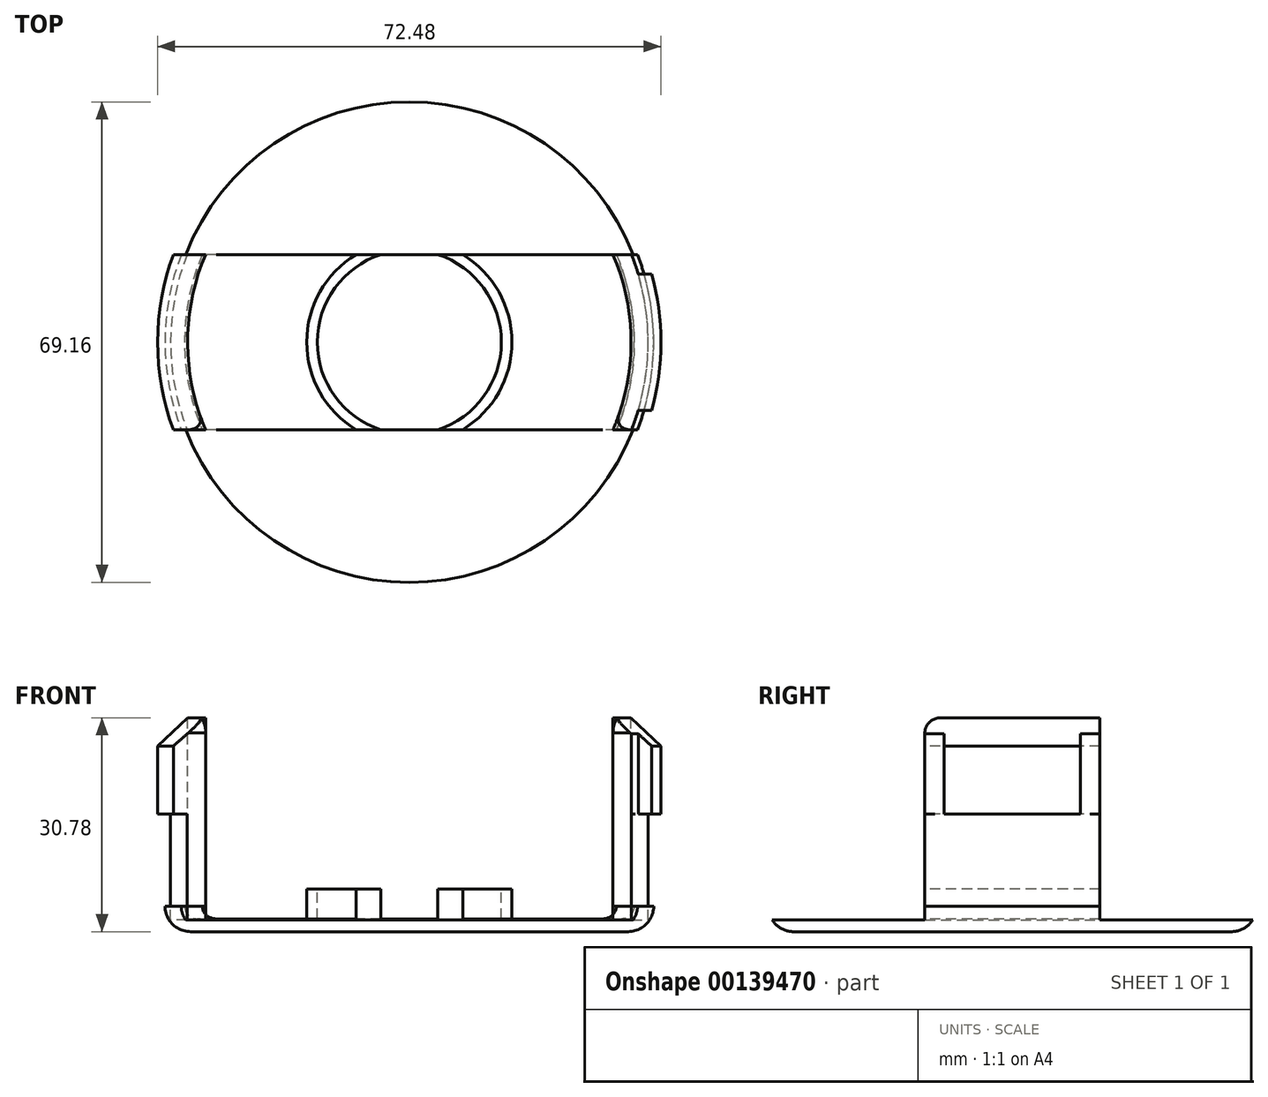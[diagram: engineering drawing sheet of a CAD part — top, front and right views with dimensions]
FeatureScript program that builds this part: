
annotation { "Feature Type Name" : "Feature", "Feature Type Description" : "" }
export const myFeature = defineFeature(function(context is Context, id is Id, definition is map)
    precondition{}
    {
        {
            var Q0;
            Q0=qCreatedBy(makeId("Front.planeOp"),FACE);
            var sketch = newSketch(context, id + "F0", { "sketchPlane" : qUnion([Q0])});
            skLineSegment(sketch, "E0.top", {"start": v(34, 4.4) * mm, "end": v(32.36, 4.4) * mm});
            skLineSegment(sketch, "E0.right", {"start": v(32.36, 0) * mm, "end": v(32.36, 4.4) * mm});
            skPoint(sketch, "E1", {"position": v(0, -3.68) * mm});
            skLineSegment(sketch, "E2", {"start": v(0, -3.68) * mm, "end": v(31.5, -3.68) * mm});
            skLineSegment(sketch, "E3", {"start": v(35.18, 0) * mm, "end": v(35.18, 0) * mm});
            skLineSegment(sketch, "E4", {"start": v(0, -3.68) * mm, "end": v(0, -1.84) * mm});
            skLineSegment(sketch, "E5", {"start": v(0, -1.84) * mm, "end": v(13.25, -1.84) * mm});
            skPoint(sketch, "E5.endSnap0", {"position": v(35.18, -1.84) * mm});
            skLineSegment(sketch, "E6.trimOffspring", {"start": v(14.77, -1.84) * mm, "end": v(30.53, -1.84) * mm});
            skPoint(sketch, "E7.visualSharp", {"position": v(35.18, -3.68) * mm});
            skArc(sketch, "E7.filletArc", {"start": v(31.5, -3.68) * mm, "mid": v(34.1, -2.6) * mm, "end": v(35.18, 0) * mm});
            skPoint(sketch, "E8.visualSharp", {"position": v(32.36, -1.84) * mm});
            skLineSegment(sketch, "E9", {"start": v(35.18, 0) * mm, "end": v(34, 0) * mm});
            skLineSegment(sketch, "E10", {"start": v(34, 0) * mm, "end": v(34, 4.4) * mm});
            skLineSegment(sketch, "E11", {"start": v(0, 4.4) * mm, "end": v(0, -3.68) * mm, "construction": true});
            skLineSegment(sketch, "E12", {"start": v(34, 3.6) * mm, "end": v(0, 3.6) * mm, "construction": true});
            skArc(sketch, "E13", {"start": v(30.53, -1.84) * mm, "mid": v(31.83, -1.3) * mm, "end": v(32.36, 0) * mm});
            skLineSegment(sketch, "E14", {"start": v(13.25, 2.46) * mm, "end": v(14.77, 2.46) * mm});
            skLineSegment(sketch, "E15", {"start": v(13.25, 2.46) * mm, "end": v(13.25, -1.84) * mm});
            skLineSegment(sketch, "E16", {"start": v(14.77, 2.46) * mm, "end": v(14.77, -1.84) * mm});
            skSolve(sketch);
        }
        {
            var Q0;
            Q0=makeQuery(id+"F0.imprint","IMPRINT",FACE,{"disambiguationData":[TD([[makeQuery(id+"F0.imprint","IMPRINT",EDGE,{"derivedFrom":sQuery(id+"F0.wireOp",EDGE,"E0.top")}),1.0]])]});
            var Q1;
            Q1=sQuery(id+"F0.wireOp",EDGE,"E11");
            revolve(context, id + "F1", {"entities" : qUnion([Q0]), "axis" : qUnion([Q1]), "revolveType" : RevolveType.FULL});
        }
        {
            var Q0;
            Q0=qCreatedBy(makeId("Top.planeOp"),FACE);
            var sketch = newSketch(context, id + "F2", { "sketchPlane" : qUnion([Q0])});
            skLineSegment(sketch, "E17", {"start": v(-42.99, 0) * mm, "end": v(-42.99, 15.25) * mm});
            skLineSegment(sketch, "E18", {"start": v(-19.65, 0) * mm, "end": v(-19.65, -15.25) * mm});
            skLineSegment(sketch, "E19", {"start": v(-19.65, -15.25) * mm, "end": v(-42.99, -15.25) * mm});
            skLineSegment(sketch, "E20", {"start": v(-42.99, -15.25) * mm, "end": v(-42.99, 0) * mm});
            skLineSegment(sketch, "E21", {"start": v(-42.99, 15.25) * mm, "end": v(-19.65, 15.25) * mm});
            skLineSegment(sketch, "E22", {"start": v(-19.65, 15.25) * mm, "end": v(-19.65, 0) * mm});
            skLineSegment(sketch, "E23.MirrorCS", {"start": v(42.99, 15.25) * mm, "end": v(19.65, 15.25) * mm});
            skLineSegment(sketch, "E24.MirrorCS", {"start": v(19.65, 15.25) * mm, "end": v(19.65, 0) * mm});
            skLineSegment(sketch, "E25.MirrorCS", {"start": v(42.99, 0) * mm, "end": v(42.99, 15.25) * mm});
            skLineSegment(sketch, "E26.MirrorCS", {"start": v(42.99, -15.25) * mm, "end": v(42.99, 0) * mm});
            skLineSegment(sketch, "E27.MirrorCS", {"start": v(19.65, -15.25) * mm, "end": v(42.99, -15.25) * mm});
            skLineSegment(sketch, "E28.MirrorCS", {"start": v(19.65, 0) * mm, "end": v(19.65, -15.25) * mm});
            skSolve(sketch);
        }
        {
            var Q0;
            Q0=makeQuery(id+"F2.imprint","IMPRINT",FACE,{"disambiguationData":[TD([[makeQuery(id+"F2.imprint","IMPRINT",EDGE,{"derivedFrom":sQuery(id+"F2.wireOp",EDGE,"E17")}),-1.0]])]});
            var Q1;
            Q1=makeQuery(id+"F2.imprint","IMPRINT",FACE,{"disambiguationData":[TD([[makeQuery(id+"F2.imprint","IMPRINT",EDGE,{"derivedFrom":sQuery(id+"F2.wireOp",EDGE,"E23.MirrorCS")}),1.0]])]});
            extrude(context, id + "F3", {"entities" : qUnion([Q0, Q1]), "operationType" : NewBodyOperationType.REMOVE, "endBound" : BoundingType.THROUGH_ALL, "depth" : 25 * mm});
        }
        {
            var Q0;
            Q0=qCreatedBy(makeId("Front.planeOp"),FACE);
            var sketch = newSketch(context, id + "F4", { "sketchPlane" : qUnion([Q0])});
            skLineSegment(sketch, "E29.left", {"start": v(34.38, 0) * mm, "end": v(34.38, 13.22) * mm});
            skLineSegment(sketch, "E29.right", {"start": v(31.92, -1.9) * mm, "end": v(31.92, 27.1) * mm});
            skLineSegment(sketch, "E30.bottom", {"start": v(34.38, 13.22) * mm, "end": v(36.24, 13.22) * mm});
            skLineSegment(sketch, "E30.right", {"start": v(36.24, 13.22) * mm, "end": v(36.24, 23.05) * mm});
            skLineSegment(sketch, "E31", {"start": v(31.92, 27.1) * mm, "end": v(36.24, 23.05) * mm});
            skLineSegment(sketch, "E32", {"start": v(0, 35.2) * mm, "end": v(0, 1.71) * mm, "construction": true});
            skLineSegment(sketch, "E33", {"start": v(34.38, 8.25) * mm, "end": v(0, 8.25) * mm, "construction": true});
            skLineSegment(sketch, "E34", {"start": v(36.24, 18.13) * mm, "end": v(31.92, 18.13) * mm, "construction": true});
            skLineSegment(sketch, "E35", {"start": v(34.38, 0) * mm, "end": v(34.38, -2) * mm});
            skLineSegment(sketch, "E36", {"start": v(34.38, -2) * mm, "end": v(31.92, -2) * mm});
            skLineSegment(sketch, "E37", {"start": v(31.92, -2) * mm, "end": v(31.92, -1.9) * mm});
            skSolve(sketch);
        }
        {
            var Q0;
            Q0=makeQuery(id+"F4.imprint","IMPRINT",FACE,{"disambiguationData":[TD([[makeQuery(id+"F4.imprint","IMPRINT",EDGE,{"derivedFrom":sQuery(id+"F4.wireOp",EDGE,"E29.left")}),1.0]])]});
            var Q1;
            Q1=sQuery(id+"F4.wireOp",EDGE,"E32");
            revolve(context, id + "F5", {"entities" : qUnion([Q0]), "axis" : qUnion([Q1]), "revolveType" : RevolveType.FULL});
        }
        {
            var Q0;
            Q0=makeQuery(id+"F5.opRevolve","SWEPT_FACE",FACE,{"disambiguationData":[OSD([sQuery(id+"F4.wireOp",EDGE,"E36")])]});
            var sketch = newSketch(context, id + "F6", { "sketchPlane" : qUnion([Q0])});
            skLineSegment(sketch, "E38.bottom", {"start": v(-47.17, -12.61) * mm, "end": v(51.45, -12.61) * mm});
            skLineSegment(sketch, "E38.top", {"start": v(-47.17, -53.6) * mm, "end": v(51.45, -53.6) * mm});
            skLineSegment(sketch, "E38.left", {"start": v(-47.17, -12.61) * mm, "end": v(-47.17, -53.6) * mm});
            skLineSegment(sketch, "E38.right", {"start": v(51.45, -12.6) * mm, "end": v(51.45, -53.6) * mm});
            skLineSegment(sketch, "E39", {"start": v(51.45, 0) * mm, "end": v(51.45, 0) * mm});
            skLineSegment(sketch, "E40.MirrorCS", {"start": v(-47.17, 12.6) * mm, "end": v(51.45, 12.61) * mm});
            skLineSegment(sketch, "E41.MirrorCS", {"start": v(-47.17, 53.6) * mm, "end": v(51.45, 53.6) * mm});
            skLineSegment(sketch, "E42.MirrorCS", {"start": v(51.45, 12.61) * mm, "end": v(51.45, 53.6) * mm});
            skLineSegment(sketch, "E43.MirrorCS", {"start": v(-47.17, 12.6) * mm, "end": v(-47.17, 53.6) * mm});
            skLineSegment(sketch, "E44", {"start": v(51.45, -12.61) * mm, "end": v(51.45, 0) * mm});
            skLineSegment(sketch, "E45", {"start": v(51.45, 12.61) * mm, "end": v(51.45, 0) * mm});
            skSolve(sketch);
        }
        {
            var Q0;
            {var subQ0=sQuery(id+"F6.wireOp",EDGE,"E40.MirrorCS");var subQ1=sQuery(id+"F4.wireOp",EDGE,"E36");var subQ2=makeQuery(id+"F5.opRevolve","SWEPT_EDGE",EDGE,{"disambiguationData":[OSD([sQuery(id+"F4.wireOp",EDGE,"E35"),subQ1])]});var subQ3=makeQuery(id+"F6.imprint","INTERSECT",VERTEX,{"disambiguationData":[OD(0.0)],"derivedFrom":[subQ2,subQ0]});Q0=makeQuery(id+"F6.imprint","IMPRINT",FACE,{"disambiguationData":[TD([[makeQuery(id+"F6.imprint","IMPRINT",EDGE,{"disambiguationData":[TD([[subQ3,-1.0]])],"derivedFrom":subQ0}),1.0]])]});}
            var Q1;
            {var subQ0=sQuery(id+"F6.wireOp",EDGE,"E40.MirrorCS");var subQ1=makeQuery(id+"F5.opRevolve","SWEPT_EDGE",EDGE,{"disambiguationData":[OSD([sQuery(id+"F4.wireOp",EDGE,"E36"),sQuery(id+"F4.wireOp",EDGE,"E37")])]});var subQ2=makeQuery(id+"F6.imprint","INTERSECT",VERTEX,{"disambiguationData":[OD(0.0)],"derivedFrom":[subQ1,subQ0]});Q1=makeQuery(id+"F6.imprint","IMPRINT",FACE,{"disambiguationData":[TD([[makeQuery(id+"F6.imprint","IMPRINT",EDGE,{"disambiguationData":[TD([[subQ2,-1.0]])],"derivedFrom":subQ0}),1.0]])]});}
            var Q2;
            Q2=makeQuery(id+"F6.imprint","IMPRINT",FACE,{"disambiguationData":[TD([[makeQuery(id+"F6.imprint","IMPRINT",EDGE,{"derivedFrom":sQuery(id+"F6.wireOp",EDGE,"E41.MirrorCS")}),-1.0]])]});
            var Q3;
            Q3=makeQuery(id+"F6.imprint","IMPRINT",FACE,{"disambiguationData":[TD([[makeQuery(id+"F6.imprint","IMPRINT",EDGE,{"derivedFrom":sQuery(id+"F6.wireOp",EDGE,"E38.top")}),1.0]])]});
            var Q4;
            {var subQ0=sQuery(id+"F6.wireOp",EDGE,"E38.bottom");var subQ1=sQuery(id+"F4.wireOp",EDGE,"E36");var subQ2=makeQuery(id+"F5.opRevolve","SWEPT_EDGE",EDGE,{"disambiguationData":[OSD([sQuery(id+"F4.wireOp",EDGE,"E35"),subQ1])]});var subQ3=makeQuery(id+"F6.imprint","INTERSECT",VERTEX,{"disambiguationData":[OD(0.0)],"derivedFrom":[subQ2,subQ0]});Q4=makeQuery(id+"F6.imprint","IMPRINT",FACE,{"disambiguationData":[TD([[makeQuery(id+"F6.imprint","IMPRINT",EDGE,{"disambiguationData":[TD([[subQ3,-1.0]])],"derivedFrom":subQ0}),-1.0]])]});}
            var Q5;
            {var subQ0=sQuery(id+"F6.wireOp",EDGE,"E38.bottom");var subQ1=makeQuery(id+"F5.opRevolve","SWEPT_EDGE",EDGE,{"disambiguationData":[OSD([sQuery(id+"F4.wireOp",EDGE,"E36"),sQuery(id+"F4.wireOp",EDGE,"E37")])]});var subQ2=makeQuery(id+"F6.imprint","INTERSECT",VERTEX,{"disambiguationData":[OD(0.0)],"derivedFrom":[subQ1,subQ0]});Q5=makeQuery(id+"F6.imprint","IMPRINT",FACE,{"disambiguationData":[TD([[makeQuery(id+"F6.imprint","IMPRINT",EDGE,{"disambiguationData":[TD([[subQ2,-1.0]])],"derivedFrom":subQ0}),-1.0]])]});}
            extrude(context, id + "F7", {"entities" : qUnion([Q0, Q1, Q2, Q3, Q4, Q5]), "operationType" : NewBodyOperationType.REMOVE, "endBound" : BoundingType.THROUGH_ALL, "oppositeDirection" : true, "depth" : 100 * mm});
        }
        {
            var Q0;
            Q0=makeQuery(id+"F7.boolean.opBoolean","SPLIT",FACE,{"disambiguationData":[OD(1.0)],"derivedFrom":makeQuery(id+"F5.opRevolve","SWEPT_FACE",FACE,{"disambiguationData":[OSD([sQuery(id+"F4.wireOp",EDGE,"E30.bottom")])]})});
            var sketch = newSketch(context, id + "F8", { "sketchPlane" : qUnion([Q0])});
            skLineSegment(sketch, "E46", {"start": v(32.95, -9.81) * mm, "end": v(40.92, -9.81) * mm});
            skPoint(sketch, "E47", {"position": v(32.52, -11.17) * mm});
            skPoint(sketch, "E48", {"position": v(31.98, -12.61) * mm});
            skFitSpline(sketch, "E49", {"points": [v(31.98, -12.61) * mm, v(32.52, -11.17) * mm, v(32.95, -9.81) * mm], "startDerivative": vector(0.8, 2.36) * mm, "endDerivative": vector(0.75, 2.45) * mm});
            skLineSegment(sketch, "E50", {"start": v(31.98, -12.61) * mm, "end": v(40.92, -12.61) * mm});
            skLineSegment(sketch, "E51", {"start": v(40.92, -12.61) * mm, "end": v(40.92, -9.81) * mm});
            skPoint(sketch, "E52.MirrorP", {"position": v(32.52, 11.17) * mm});
            skLineSegment(sketch, "E53.MirrorCS", {"start": v(31.98, 12.61) * mm, "end": v(40.92, 12.61) * mm});
            skLineSegment(sketch, "E54.MirrorCS", {"start": v(40.92, 12.61) * mm, "end": v(40.92, 9.81) * mm});
            skPoint(sketch, "E55.MirrorP", {"position": v(31.98, 12.61) * mm});
            skLineSegment(sketch, "E56.MirrorCS", {"start": v(32.95, 9.81) * mm, "end": v(40.92, 9.81) * mm});
            skFitSpline(sketch, "E57.MirrorCS", {"points": [v(31.98, 12.61) * mm, v(32.52, 11.17) * mm, v(32.95, 9.81) * mm], "startDerivative": vector(0.8, -2.36) * mm, "endDerivative": vector(0.75, -2.45) * mm});
            skFitSpline(sketch, "E58.MirrorCS", {"points": [v(31.98, 12.61) * mm, v(32.52, 11.17) * mm, v(32.95, 9.81) * mm], "startDerivative": vector(0.8, -2.36) * mm, "endDerivative": vector(0.75, -2.45) * mm});
            skFitSpline(sketch, "E59.MirrorCS", {"points": [v(31.98, 12.61) * mm, v(32.52, 11.17) * mm, v(32.95, 9.81) * mm], "startDerivative": vector(0.8, -2.36) * mm, "endDerivative": vector(0.75, -2.45) * mm});
            skLineSegment(sketch, "E60.MirrorCS", {"start": v(-31.98, -12.61) * mm, "end": v(-40.92, -12.61) * mm});
            skLineSegment(sketch, "E61.MirrorCS", {"start": v(-40.92, -12.61) * mm, "end": v(-40.92, -9.81) * mm});
            skFitSpline(sketch, "E62.MirrorCS", {"points": [v(-31.98, -12.61) * mm, v(-32.52, -11.17) * mm, v(-32.95, -9.81) * mm], "startDerivative": vector(-0.8, 2.36) * mm, "endDerivative": vector(-0.75, 2.45) * mm});
            skLineSegment(sketch, "E63.MirrorCS", {"start": v(-32.95, 9.81) * mm, "end": v(-40.92, 9.81) * mm});
            skLineSegment(sketch, "E64.MirrorCS", {"start": v(-32.95, -9.81) * mm, "end": v(-40.92, -9.81) * mm});
            skLineSegment(sketch, "E65.MirrorCS", {"start": v(-31.98, 12.61) * mm, "end": v(-40.92, 12.61) * mm});
            skLineSegment(sketch, "E66.MirrorCS", {"start": v(-40.92, 12.61) * mm, "end": v(-40.92, 9.81) * mm});
            skFitSpline(sketch, "E67.MirrorCS", {"points": [v(-31.98, 12.61) * mm, v(-32.52, 11.17) * mm, v(-32.95, 9.81) * mm], "startDerivative": vector(-0.8, -2.36) * mm, "endDerivative": vector(-0.75, -2.45) * mm});
            skSolve(sketch);
        }
        {
            var Q0;
            Q0=makeQuery(id+"F8.imprint","IMPRINT",FACE,{"disambiguationData":[TD([[makeQuery(id+"F8.imprint","IMPRINT",EDGE,{"derivedFrom":sQuery(id+"F8.wireOp",EDGE,"E60.MirrorCS")}),-1.0]])]});
            var Q1;
            Q1=makeQuery(id+"F8.imprint","IMPRINT",FACE,{"disambiguationData":[TD([[makeQuery(id+"F8.imprint","IMPRINT",EDGE,{"derivedFrom":sQuery(id+"F8.wireOp",EDGE,"E63.MirrorCS")}),-1.0]])]});
            extrude(context, id + "F9", {"entities" : qUnion([Q0, Q1]), "operationType" : NewBodyOperationType.REMOVE, "oppositeDirection" : true, "depth" : 25 * mm});
        }
        {
            var Q0;
            {var subQ1=sQuery(id+"F8.wireOp",EDGE,"E53.MirrorCS");Q0=makeQuery(id+"F8.imprint","IMPRINT",FACE,{"disambiguationData":[TD([[makeQuery(id+"F8.imprint","IMPRINT",EDGE,{"derivedFrom":subQ1}),-1.0]])]});}
            var Q1;
            {var subQ0=sQuery(id+"F8.wireOp",EDGE,"E50");Q1=makeQuery(id+"F8.imprint","IMPRINT",FACE,{"disambiguationData":[TD([[makeQuery(id+"F8.imprint","IMPRINT",EDGE,{"derivedFrom":subQ0}),1.0]])]});}
            var Q2;
            {var subQ0=sQuery(id+"F8.wireOp",EDGE,"E59.MirrorCS");var subQ1=sQuery(id+"F8.wireOp",EDGE,"E56.MirrorCS");var subQ2=makeQuery(id+"F8.imprint","INTERSECT",VERTEX,{"derivedFrom":[subQ1,subQ0]});Q2=makeQuery(id+"F8.imprint","IMPRINT",FACE,{"disambiguationData":[TD([[makeQuery(id+"F8.imprint","IMPRINT",EDGE,{"disambiguationData":[TD([[subQ2,-1.0]])],"derivedFrom":subQ1}),1.0]])]});}
            var Q3;
            {var subQ0=sQuery(id+"F8.wireOp",EDGE,"E49");var subQ1=sQuery(id+"F8.wireOp",EDGE,"E46");var subQ2=makeQuery(id+"F8.imprint","INTERSECT",VERTEX,{"derivedFrom":[subQ1,subQ0]});Q3=makeQuery(id+"F8.imprint","IMPRINT",FACE,{"disambiguationData":[TD([[makeQuery(id+"F8.imprint","IMPRINT",EDGE,{"disambiguationData":[TD([[subQ2,-1.0]])],"derivedFrom":subQ1}),-1.0]])]});}
            extrude(context, id + "F10", {"entities" : qUnion([Q0, Q1, Q2, Q3]), "operationType" : NewBodyOperationType.REMOVE, "endBound" : BoundingType.THROUGH_ALL, "oppositeDirection" : true, "depth" : 25 * mm});
        }
        {
            var Q0;
            Q0=qCreatedBy(makeId("Right.planeOp"),FACE);
            var sketch = newSketch(context, id + "F11", { "sketchPlane" : qUnion([Q0])});
            skArc(sketch, "E68.MirrorC", {"start": v(10.4, 27.09) * mm, "mid": v(11.95, 26.48) * mm, "end": v(12.6, 24.97) * mm});
            skLineSegment(sketch, "E69", {"start": v(10.4, 27.09) * mm, "end": v(10.4, 27.95) * mm});
            skLineSegment(sketch, "E70", {"start": v(10.4, 27.95) * mm, "end": v(13.33, 27.94) * mm});
            skLineSegment(sketch, "E71", {"start": v(13.33, 27.94) * mm, "end": v(13.33, 24.97) * mm});
            skLineSegment(sketch, "E72", {"start": v(13.33, 24.97) * mm, "end": v(12.6, 24.97) * mm});
            skLineSegment(sketch, "E73.MirrorCS", {"start": v(-13.33, 24.97) * mm, "end": v(-12.6, 24.97) * mm});
            skLineSegment(sketch, "E74.MirrorCS", {"start": v(-10.4, 27.09) * mm, "end": v(-10.4, 27.95) * mm});
            skLineSegment(sketch, "E75.MirrorCS", {"start": v(-10.4, 27.95) * mm, "end": v(-13.33, 27.94) * mm});
            skLineSegment(sketch, "E76.MirrorCS", {"start": v(-13.33, 27.94) * mm, "end": v(-13.33, 24.97) * mm});
            skArc(sketch, "E77.MirrorCS", {"start": v(-10.4, 27.09) * mm, "mid": v(-11.95, 26.48) * mm, "end": v(-12.6, 24.97) * mm});
            skSolve(sketch);
        }
        {
            var Q0;
            Q0=makeQuery(id+"F11.imprint","IMPRINT",FACE,{"disambiguationData":[TD([[makeQuery(id+"F11.imprint","IMPRINT",EDGE,{"derivedFrom":sQuery(id+"F11.wireOp",EDGE,"E68.MirrorC")}),1.0]])]});
            var Q1;
            Q1=makeQuery(id+"F11.imprint","IMPRINT",FACE,{"disambiguationData":[TD([[makeQuery(id+"F11.imprint","IMPRINT",EDGE,{"derivedFrom":sQuery(id+"F11.wireOp",EDGE,"E73.MirrorCS")}),1.0]])]});
            extrude(context, id + "F12", {"entities" : qUnion([Q0, Q1]), "operationType" : NewBodyOperationType.REMOVE, "endBound" : BoundingType.SYMMETRIC, "depth" : 100 * mm});
        }
    });
